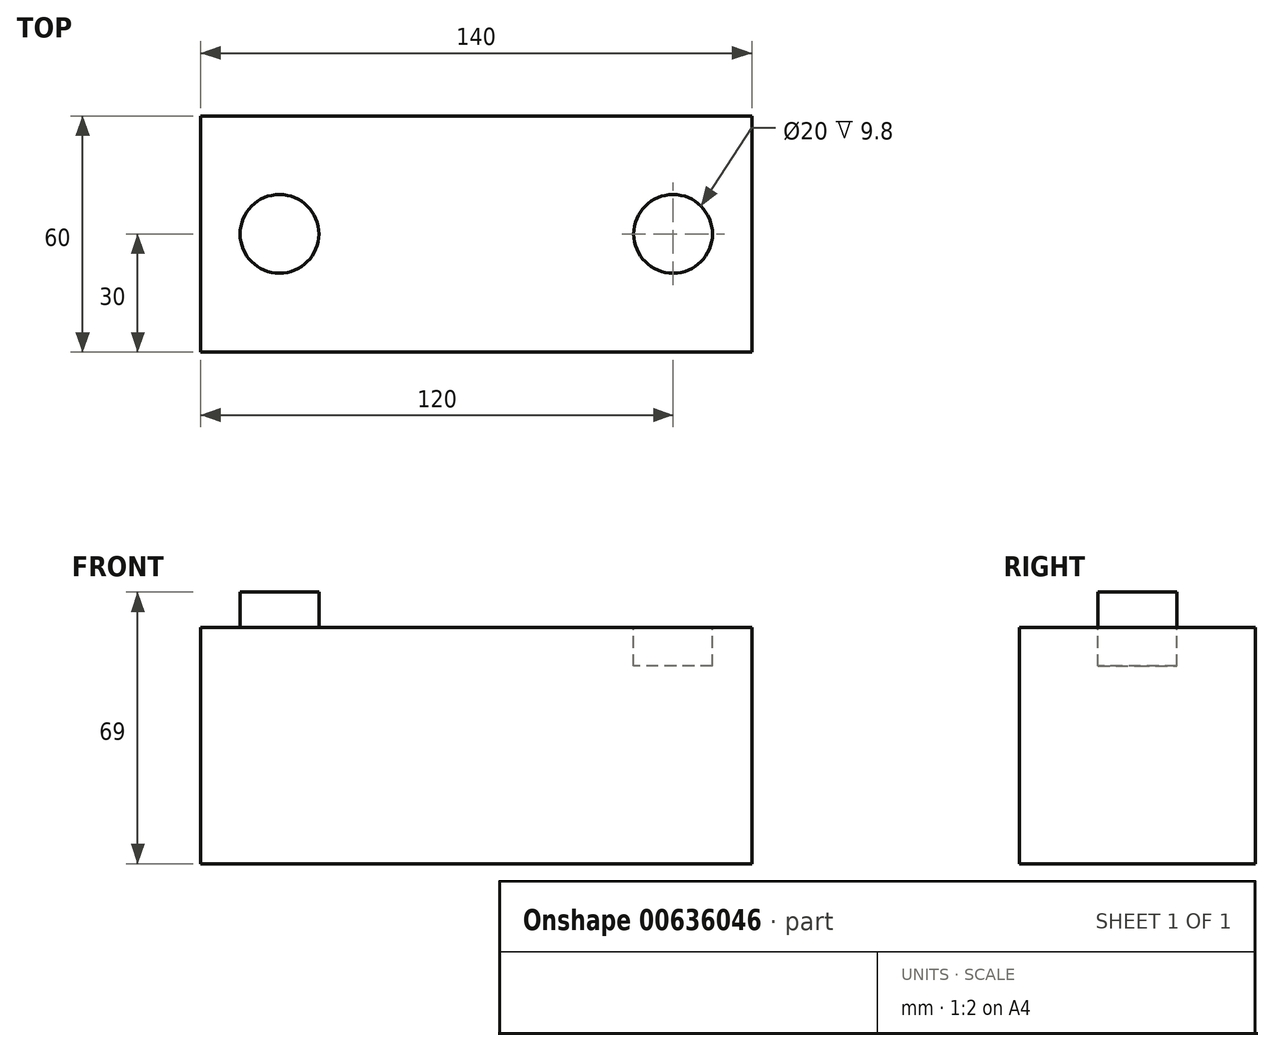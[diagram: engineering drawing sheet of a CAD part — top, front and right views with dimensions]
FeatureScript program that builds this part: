
annotation { "Feature Type Name" : "Feature", "Feature Type Description" : "" }
export const myFeature = defineFeature(function(context is Context, id is Id, definition is map)
    precondition{}
    {
        {
            var Q0;
            Q0=qCreatedBy(makeId("Top.planeOp"),FACE);
            var sketch = newSketch(context, id + "F0", { "sketchPlane" : qUnion([Q0])});
            skLineSegment(sketch, "E0.bottom", {"start": v(70, -30) * mm, "end": v(-70, -30) * mm});
            skLineSegment(sketch, "E0.top", {"start": v(70, 30) * mm, "end": v(-70, 30) * mm});
            skLineSegment(sketch, "E0.left", {"start": v(70, -30) * mm, "end": v(70, 30) * mm});
            skLineSegment(sketch, "E0.right", {"start": v(-70, -30) * mm, "end": v(-70, 30) * mm});
            skPoint(sketch, "E0.middle", {"position": v(0, 0) * mm});
            skSolve(sketch);
        }
        {
            var Q0;
            Q0 = qSketchRegion(id + "F0", true);
            extrude(context, id + "F1", {"entities" : qUnion([Q0]), "depth" : 60 * mm, "offsetDistance" : 25 * mm});
        }
        {
            var Q0;
            Q0=makeQuery(id+"F1.opExtrude","CAP_FACE",FACE,{"disambiguationData":[OSD([sQuery(id+"F0.wireOp",EDGE,"E0.bottom"),sQuery(id+"F0.wireOp",EDGE,"E0.top"),sQuery(id+"F0.wireOp",EDGE,"E0.left"),sQuery(id+"F0.wireOp",EDGE,"E0.right")])],"isStart":false});
            var sketch = newSketch(context, id + "F2", { "sketchPlane" : qUnion([Q0])});
            skLineSegment(sketch, "E1", {"start": v(-70, 0) * mm, "end": v(-50, 0) * mm});
            skLineSegment(sketch, "E2", {"start": v(70, 0) * mm, "end": v(50, 0) * mm});
            skPoint(sketch, "E2.endSnap0", {"position": v(70, 0) * mm});
            skSolve(sketch);
        }
        {
            var Q0;
            Q0=qCreatedBy(makeId("Top.planeOp"),FACE);
            var sketch = newSketch(context, id + "F3", { "sketchPlane" : qUnion([Q0])});
            skCircle(sketch, "E3", {"center": v(-50, 0) * mm, "radius": 10 * mm});
            skPoint(sketch, "E3.first.point", {"position": v(-60, 0) * mm});
            skPoint(sketch, "E3.second.point", {"position": v(-40, 0) * mm});
            skPoint(sketch, "E3.third.point", {"position": v(-46.02, -9.17) * mm});
            skSolve(sketch);
        }
        {
            var Q0;
            {var subQ3=makeQuery(id+"F1.opExtrude","CAP_EDGE",EDGE,{"disambiguationData":[OSD([sQuery(id+"F0.wireOp",EDGE,"E0.bottom")])],"isStart":false});Q0=makeQuery(id+"F2.imprint","IMPRINT",FACE,{"disambiguationData":[TD([[makeQuery(id+"F2.imprint","IMPRINT",EDGE,{"derivedFrom":subQ3}),-1.0]])]});}
            var sketch = newSketch(context, id + "F4", { "sketchPlane" : qUnion([Q0])});
            skCircle(sketch, "E4", {"center": v(50, 0) * mm, "radius": 10 * mm});
            skPoint(sketch, "E4.first.point", {"position": v(60, 0) * mm});
            skPoint(sketch, "E4.second.point", {"position": v(49.23, 9.97) * mm});
            skPoint(sketch, "E4.third.point", {"position": v(40, 0) * mm});
            skSolve(sketch);
        }
        {
            var Q0;
            Q0 = qSketchRegion(id + "F3", true);
            extrude(context, id + "F5", {"entities" : qUnion([Q0]), "operationType" : NewBodyOperationType.ADD, "depth" : 69 * mm, "offsetDistance" : 25 * mm});
        }
        {
            var Q0;
            Q0 = qSketchRegion(id + "F4", true);
            extrude(context, id + "F6", {"entities" : qUnion([Q0]), "operationType" : NewBodyOperationType.REMOVE, "oppositeDirection" : true, "depth" : 9.8 * mm, "offsetDistance" : 25 * mm});
        }
    });
